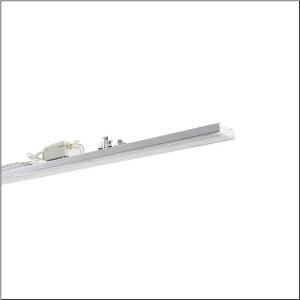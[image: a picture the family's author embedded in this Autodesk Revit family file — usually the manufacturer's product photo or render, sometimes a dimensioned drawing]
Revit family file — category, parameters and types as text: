
# Revit family: licross_r__21_recessed_ho_52te11dv4lxs_d195
name_source: partatom
category: Lighting Fixtures
units: mm (PartAtom-declared; Revit-internal decimal feet)

## family parameters
Cut with Voids When Loaded = No
Host = Face
Light Source = No
Part Type = Normal
Room Calculation Point = No
Round Connector Dimension = Use Diameter
Shared = No

## types (1)
- --- (1 x LED, 20000 lm, 110.1 W, 4000K)
    Apparent Load = 110 VA
    CIE Flux Codes = 87 95 99 100 100
    Color Rendering = 80
    Color Temperature = 4000K
    Default Elevation = 1800 mm
    Description = Licross® 21 Recessed HO, luminaire insert, of sheet steel, galvanised, coil coated, white, length: 2.250mm, width: 66mm, height: 67mm, LED rated luminous flux: 20.000lm, light colour: 840, control gear: DALI 2, with plug, 5-pole, with phase selection, mains connection: 220..240V, AC, 50/60Hz, rated input power: 110W, halogen-free wiring, primary light control with lens, of plastic, primary optical cover: cover, of PMMA, light emission: direct distribution, primary light characteristic: symmetric, protection rating (complete): IP54, insulation class (complete): insulation class I (protective earthing), certification: CE, ENEC, VDE, UKCA, protection symbol: D if used in an environment with non-conductive dust loads with corresponding accessories, impact resistance: IK06, permissible ambient temperature for indoor applications: -40..+35°C, corresponds to IFS (International Featured Standards) requirements for safety and quality in the food industry, reducing of maximum allowable ambient temperature of 5°C with ceiling mounting, LABS conformity tested according to VDMA 24364:2018-05, packaging unit: 1 piece
    Height = 58 mm
    Lamp = 1 x LED
    Lamp Light Flux = 20000 lm
    Lamp Power = 110.1 W
    Lamp count = 1
    Length = 2250 mm
    Luminous efficacy = 182 lm/W
    Manufacturer = Siteco
    ModVariant = No
    Model = 52TE11DV4LXS
    Mounting Place = Ceiling
    Mounting Type = Pendant
    Number of Poles = 1
    OnlyDefault = Yes
    Power Factor = 1
    Product Name = Licross® 21 Recessed HO
    Product group = luminaire insert
    ProductGroupID = 901
    Protection Class = Protection class I
    Protection Degree = IP 54
    RLX_Detail_Level = 1
    RLX_Emergency_Light_Flux = 0 lm
    RLX_Emergency_Type = 0
    RLX_Emergency_Type_DB = No
    RlxData = <blob elided: 29397 chars, md5=6f893361>
    Socket = socket
    Standby Power = 0 W
    System Light Flux = 20000 lm
    System Power = 110 W
    Type Comments = factory setting: luminous flux: 100 % | dim-lin: 254 | 426 mA
    Type Image = l_1296930.jpg
    URL = http://relux.com
    VarID = @adj_058947
    Voltage = 0 V
    Weight = 0.00 kg
    Width = 66 mm

## geometry (parser evidence)
native form markers: Blend x4, Sweep x10
no freeform markers — native parametric forms only
